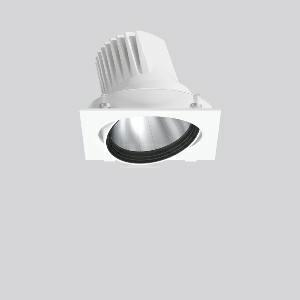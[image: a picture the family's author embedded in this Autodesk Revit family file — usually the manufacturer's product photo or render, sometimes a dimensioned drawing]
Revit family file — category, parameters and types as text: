
# Revit family: magcardo_maxi_722208_002_76_7b7e
name_source: partatom
category: Lighting Fixtures
units: mm (PartAtom-declared; Revit-internal decimal feet)

## family parameters
Cut with Voids When Loaded = No
Host = Face
Light Source = No
Part Type = Normal
Room Calculation Point = No
Round Connector Dimension = Use Diameter
Shared = No

## types (1)
- MAGCARDO maxi (1 x LED Modul 920 meat+, 2250 lm, 2000)
    Apparent Load = 33 VA
    Approval mark = CE
    CIE Flux Codes = 100 100 100 100 100
    Color Rendering = 90
    Color Temperature = 2000
    Default Elevation = 1800 mm
    Description = Series: MAGCARDO maxi
Projector unit for tool-free mounting in separate recessed frame. Luminaire top: die-cast aluminium, powder-coated. Rotation range 356° and swivel range ± 35°. Inner cover prevents view into the false ceiling. Black plastic ring and recessed LED to prevent glare from the side. Optical assembly with reflector made of MIRO-Silver with 98% total light reflection for outstanding efficiency - can be changed without tools. Special LED for illumination of meat included. Magnetic click locking mechanism for quick and convenient installation without tools: insert the recessed frame (1, 2 or 3-lamp) with clamp fastener (no tools required), push the luminaire head with the base plate into the recessed frame and fix magnetically. Including separate LED converter with connecting cable 600 mm.High quality converter without flickering and stroboscopic effect. Through-wiring box (5 pole) available as accessory. The following accessories can be mounted without use of tools: interchangeable lenses, honeycomb louvre, clear and frosted diffusers, white interchangeable plastic ring.Modular design: recessed mounting frame must be ordered separately! 
Colour: traffic white, matt (RAL 9016)
Length: 172 mm
Width: 167 mm
Height: 137 mm
Recess height: 155 mm
Lamp: LED
Socket: without socket
Colour temperature: meat +
System power: 33 W
Rated luminous flux: 2250 lm
Luminous efficiency: 68 lm/W
Control gear: Converter, dimmable, DALI
Protection class: II
Type of protection: IP 20
    Height = 0 mm  [stored 0 ft]
    Lamp = 1 x LED Modul 920 meat+
    Lamp Light Flux = 2250 lm
    Lamp count = 1
    Length = 172 mm
    Lifetime = 50000 h
    Luminous efficacy = 68 lm/W
    Manufacturer = RZB
    ModVariant = No
    Model = 722208.002.76
    Mounting Place = Ceiling, Wall
    Mounting Type = Recessed
    Number of Poles = 1
    OnlyDefault = Yes
    Power Factor = 1
    Product Name = MAGCARDO maxi
    Product group = Recessed projectors
    ProductGroupID = 401
    Protection Class = Protection class II
    Protection Degree = IP 20
    RLX_Detail_Level = 1
    RLX_Emergency_Light_Flux = 0 lm
    RLX_Emergency_Type = 0
    RLX_Emergency_Type_DB = No
    RlxData = <blob elided: 40357 chars, md5=0a32b039>
    Socket = socket
    Standby Power = 0 W
    System Light Flux = 2250 lm
    System Power = 33 W
    Type Comments = Product without accessories
    Type Image = 722045.002.jpg
    URL = http://relux.com
    VarID = ---
    Voltage = 230 V
    Voltage Range = 220-240 V
    Weight = 0.00 kg
    Width = 167 mm

note: [stored X ft] marks values corroborated as IEEE doubles in the binary element streams (Revit-internal decimal feet)

## geometry (parser evidence)
native form markers: Blend x4, Sweep x10
no freeform markers — native parametric forms only
